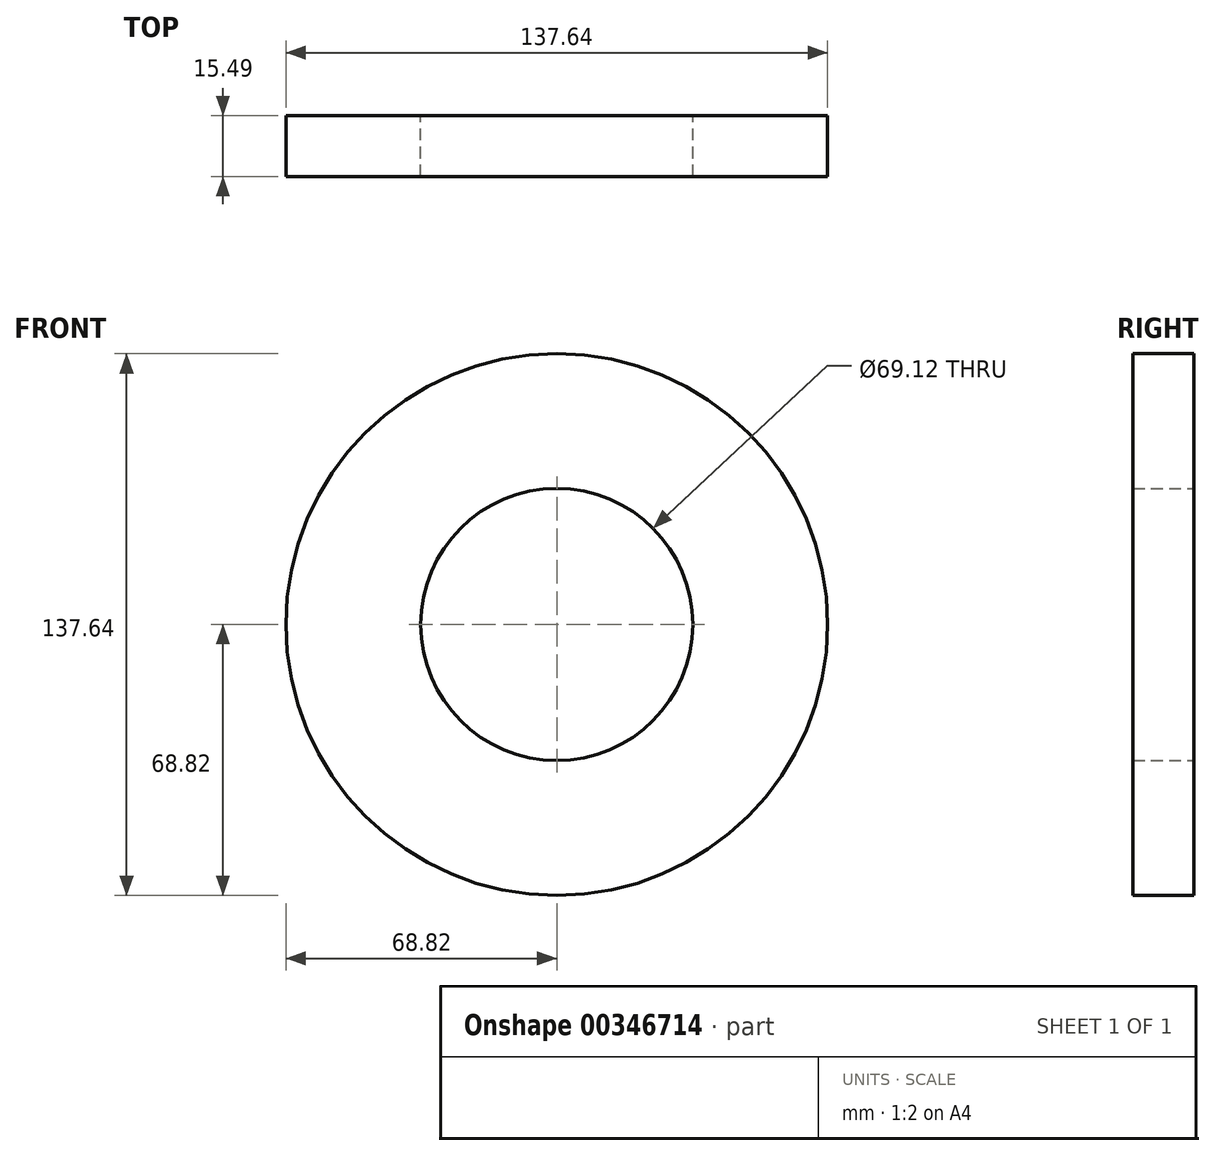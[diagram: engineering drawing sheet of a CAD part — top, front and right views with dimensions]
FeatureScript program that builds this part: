
annotation { "Feature Type Name" : "Feature", "Feature Type Description" : "" }
export const myFeature = defineFeature(function(context is Context, id is Id, definition is map)
    precondition{}
    {
        {
            var Q0;
            Q0=qCreatedBy(makeId("Front.planeOp"),FACE);
            var sketch = newSketch(context, id + "F0", { "sketchPlane" : qUnion([Q0])});
            skCircle(sketch, "E0", {"center": v(0, 0) * mm, "radius": 68.82 * mm});
            skCircle(sketch, "E1", {"center": v(0, 0) * mm, "radius": 34.56 * mm});
            skLineSegment(sketch, "E2", {"start": v(-3.72, 34.36) * mm, "end": v(3.15, 68.74) * mm});
            skLineSegment(sketch, "E3", {"start": v(1.99, 34.5) * mm, "end": v(8.73, 68.26) * mm});
            skSolve(sketch);
        }
        {
            var Q0;
            {var subQ0=sQuery(id+"F0.wireOp",EDGE,"E2");Q0=makeQuery(id+"F0.imprint","IMPRINT",FACE,{"disambiguationData":[TD([[makeQuery(id+"F0.imprint","IMPRINT",EDGE,{"derivedFrom":subQ0}),-1.0]])]});}
            var Q1;
            {var subQ0=sQuery(id+"F0.wireOp",EDGE,"E2");Q1=makeQuery(id+"F0.imprint","IMPRINT",FACE,{"disambiguationData":[TD([[makeQuery(id+"F0.imprint","IMPRINT",EDGE,{"derivedFrom":subQ0}),1.0]])]});}
            extrude(context, id + "F1", {"entities" : qUnion([Q0, Q1]), "depth" : 15.5 * mm, "hasSecondDirection" : true, "secondDirectionOppositeDirection" : false, "secondDirectionDepth" : 0 * mm});
        }
        {
            var Q0;
            Q0=qCreatedBy(makeId("Front.planeOp"),FACE);
            var sketch = newSketch(context, id + "F2", { "sketchPlane" : qUnion([Q0])});
            skLineSegment(sketch, "E4", {"start": v(-4.03, 34.25) * mm, "end": v(0, 69.07) * mm});
            skLineSegment(sketch, "E5", {"start": v(0, 34.25) * mm, "end": v(4.03, 69.07) * mm});
            skLineSegment(sketch, "E6", {"start": v(-4.03, 34.25) * mm, "end": v(0, 34.25) * mm});
            skLineSegment(sketch, "E7", {"start": v(4.03, 69.07) * mm, "end": v(0, 69.07) * mm});
            skSolve(sketch);
        }
        {
            var Q0;
            Q0=sQuery(id+"F2.wireOp",EDGE,"E4");
            var Q1;
            Q1=sQuery(id+"F2.wireOp",EDGE,"E5");
            extrude(context, id + "F3", {"bodyType" : ToolBodyType.SURFACE, "surfaceEntities" : qUnion([Q0, Q1]), "depth" : 20.07 * mm});
        }
    });
